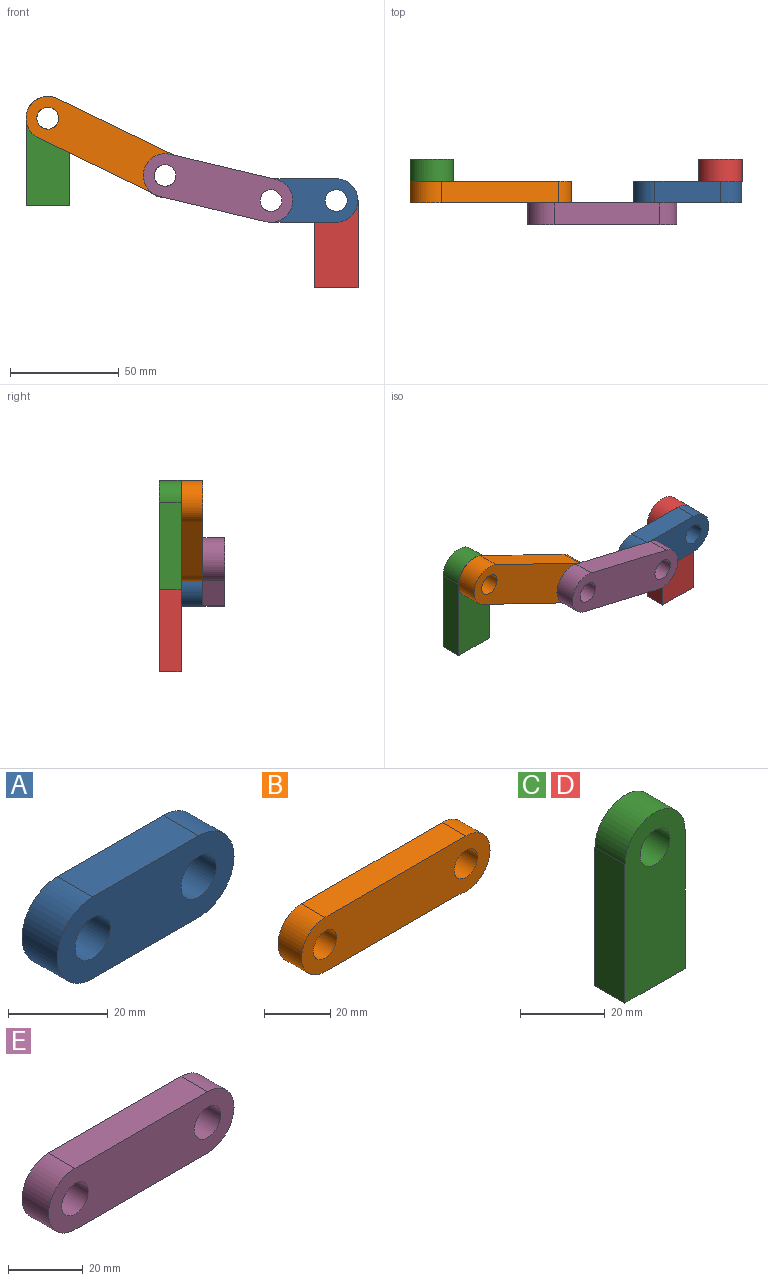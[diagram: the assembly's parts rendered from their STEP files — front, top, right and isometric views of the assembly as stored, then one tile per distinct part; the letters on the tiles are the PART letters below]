
ASSEMBLY  parts=5 mates=5
PART A: 8 faces, bbox 50x10x20 mm
  f0: cylinder r=10mm len=20mm, axis (0,1,0), area 314.2mm2, adj f1,f5,f6,f7
  f1: plane 30x10mm, normal (0,0,-1), area 300mm2, adj f0,f2,f6,f7
  f2: cylinder r=10mm len=20mm, axis (0,1,0), area 314.2mm2, adj f1,f5,f6,f7
  f3: cylinder r=5mm len=10mm, axis (0,1,0), area 314.2mm2, adj f6,f7
  f4: cylinder r=5mm len=10mm, axis (0,1,0), area 314.2mm2, adj f6,f7
  f5: plane 30x10mm, normal (0,0,1), area 300mm2, adj f0,f2,f6,f7
  f6: plane 50x20mm, normal (0,-1,0), area 757.1mm2, adj f0,f1,f2,f3,f4,f5
  f7: plane 50x20mm, normal (0,1,0), area 757.1mm2, adj f0,f1,f2,f3,f4,f5
PART B: 8 faces, bbox 80.2x10x20.5 mm
  f0: cylinder r=10mm len=20mm, axis (0,1,0), area 314.2mm2, adj f1,f5,f6,f7
  f1: plane 56.92x10mm, normal (0,0,-1), area 569.2mm2, adj f0,f2,f6,f7
  f2: cylinder r=10.24mm len=20.48mm, axis (0,1,0), area 352.9mm2, adj f1,f5,f6,f7
  f3: cylinder r=5mm len=10mm, axis (0,1,0), area 314.2mm2, adj f6,f7
  f4: cylinder r=5mm len=10mm, axis (0,1,0), area 314.2mm2, adj f6,f7
  f5: plane 60x10mm, normal (0,0,1), area 600mm2, adj f0,f2,f6,f7
  f6: plane 80.24x20.48mm, normal (0,-1,0), area 1365.6mm2, adj f0,f1,f2,f3,f4,f5
  f7: plane 80.24x20.48mm, normal (0,1,0), area 1365.6mm2, adj f0,f1,f2,f3,f4,f5
PART C: 7 faces, bbox 20x10x50 mm
  f0: plane 40x10mm, normal (1,0,0), area 400mm2, adj f1,f4,f5,f6
  f1: cylinder r=10mm len=20mm, axis (0,1,0), area 314.2mm2, adj f0,f2,f5,f6
  f2: plane 40x10mm, normal (-1,0,0), area 400mm2, adj f1,f4,f5,f6
  f3: cylinder r=5mm len=10mm, axis (0,1,0), area 314.2mm2, adj f5,f6
  f4: plane 20x10mm, normal (0,0,-1), area 200mm2, adj f0,f2,f5,f6
  f5: plane 50x20mm, normal (0,-1,0), area 878.5mm2, adj f0,f1,f2,f3,f4
  f6: plane 50x20mm, normal (0,1,0), area 878.5mm2, adj f0,f1,f2,f3,f4
PART D: same geometry as C
PART E: 8 faces, bbox 70x10x20 mm
  f0: cylinder r=10mm len=20mm, axis (0,1,0), area 314.2mm2, adj f1,f5,f6,f7
  f1: plane 50x10mm, normal (0,0,-1), area 500mm2, adj f0,f2,f6,f7
  f2: cylinder r=10mm len=20mm, axis (0,1,0), area 314.2mm2, adj f1,f5,f6,f7
  f3: cylinder r=5mm len=10mm, axis (0,1,0), area 314.2mm2, adj f6,f7
  f4: cylinder r=5mm len=10mm, axis (0,1,0), area 314.2mm2, adj f6,f7
  f5: plane 50x10mm, normal (0,0,1), area 500mm2, adj f0,f2,f6,f7
  f6: plane 70x20mm, normal (0,-1,0), area 1157.1mm2, adj f0,f1,f2,f3,f4,f5
  f7: plane 70x20mm, normal (0,1,0), area 1157.1mm2, adj f0,f1,f2,f3,f4,f5
PLACE A t=(11.62,-29.31,-7.94)mm
PLACE B rot(axis=(0,1,0),25.8deg) t=(-71.88,-29.31,21.58)mm
PLACE C t=(-90.94,-19.31,21.63)mm
PLACE D t=(41.64,-19.31,-16.18)mm
PLACE E rot(axis=(0,1,0),13.3deg) t=(0.04,-39.31,-4.51)mm
MATE revolute B.f2 <-> E.f0  axis (0,-1,0) through (-37.04,-39.31,3.56)mm
MATE revolute E.f2 <-> A.f0  axis (0,1,0) through (11.62,-39.31,-7.94)mm
MATE parallel D.f0 <-> C.f2  axis (1,0,0) through (51.62,-19.31,-27.94)mm
MATE revolute D.f1 <-> A.f2  axis (0,-1,0) through (41.62,-29.31,-7.94)mm
MATE revolute C.f1 <-> B.f0  axis (0,-1,0) through (-90.96,-29.31,29.87)mm
